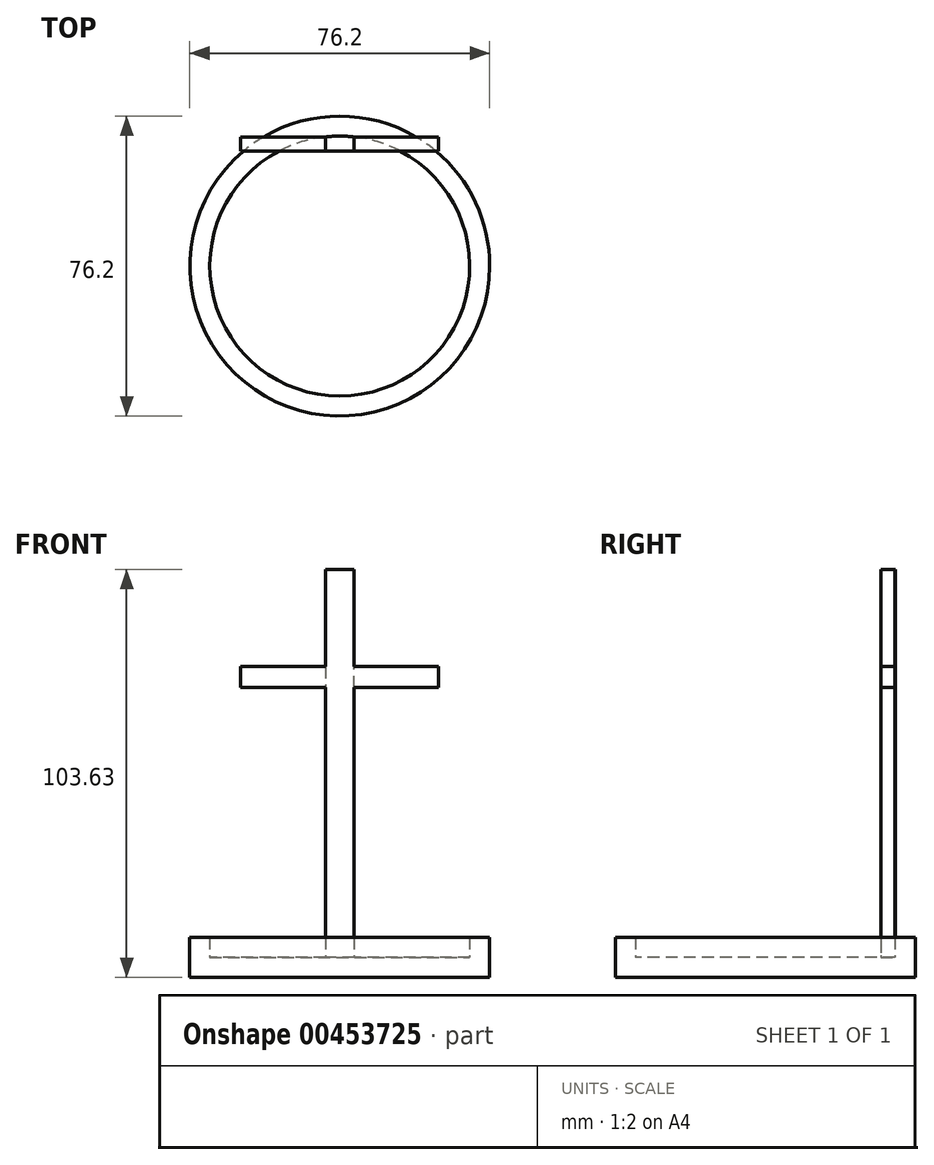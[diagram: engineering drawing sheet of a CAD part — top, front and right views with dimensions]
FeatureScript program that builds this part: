
annotation { "Feature Type Name" : "Feature", "Feature Type Description" : "" }
export const myFeature = defineFeature(function(context is Context, id is Id, definition is map)
    precondition{}
    {
        {
            var Q0;
            Q0=qCreatedBy(makeId("Top.planeOp"),FACE);
            var sketch = newSketch(context, id + "F0", { "sketchPlane" : qUnion([Q0])});
            skCircle(sketch, "E0", {"center": v(0, 0) * mm, "radius": 38.1 * mm});
            skSolve(sketch);
        }
        {
            var Q0;
            Q0=makeQuery(id+"F0.imprint","IMPRINT",FACE,{"disambiguationData":[TD([[makeQuery(id+"F0.imprint","IMPRINT",EDGE,{"derivedFrom":sQuery(id+"F0.wireOp",EDGE,"E0")}),1.0]])]});
            extrude(context, id + "F1", {"entities" : qUnion([Q0]), "depth" : 10.16 * mm});
        }
        {
            var Q0;
            Q0=makeQuery(id+"F1.opExtrude","CAP_FACE",FACE,{"disambiguationData":[OSD([sQuery(id+"F0.wireOp",EDGE,"E0")])],"isStart":false});
            shell(context, id + "F2", {"entities" : qUnion([Q0]), "thickness" : 5.08 * mm});
        }
        {
            var Q0;
            {var subQ0=sQuery(id+"F0.wireOp",EDGE,"E0");Q0=makeQuery(id+"F2.opShell","OFFSET_FACE",FACE,{"disambiguationData":[OSD([subQ0]),TDD([makeQuery(id+"F1.opExtrude","CAP_FACE",FACE,{"disambiguationData":[OSD([subQ0])],"isStart":true})])]});}
            var sketch = newSketch(context, id + "F3", { "sketchPlane" : qUnion([Q0])});
            skLineSegment(sketch, "E1.bottom", {"start": v(3.64, 29.24) * mm, "end": v(-3.64, 29.24) * mm});
            skLineSegment(sketch, "E1.top", {"start": v(3.64, 33.91) * mm, "end": v(-3.64, 33.91) * mm});
            skLineSegment(sketch, "E1.left", {"start": v(3.64, 29.24) * mm, "end": v(3.64, 33.91) * mm});
            skLineSegment(sketch, "E1.right", {"start": v(-3.64, 29.24) * mm, "end": v(-3.64, 33.91) * mm});
            skPoint(sketch, "E1.middle", {"position": v(0, 31.58) * mm});
            skSolve(sketch);
        }
        {
            var Q0;
            Q0=makeQuery(id+"F3.imprint","IMPRINT",FACE,{"disambiguationData":[TD([[makeQuery(id+"F3.imprint","IMPRINT",EDGE,{"derivedFrom":sQuery(id+"F3.wireOp",EDGE,"E1.bottom")}),-1.0]])]});
            extrude(context, id + "F4", {"entities" : qUnion([Q0]), "operationType" : NewBodyOperationType.ADD, "depth" : 98.55 * mm});
        }
        {
            var Q0;
            Q0=qCreatedBy(makeId("Right.planeOp"),FACE);
            var sketch = newSketch(context, id + "F5", { "sketchPlane" : qUnion([Q0])});
            skLineSegment(sketch, "E2.bottom", {"start": v(29.24, 73.62) * mm, "end": v(32.82, 73.62) * mm});
            skLineSegment(sketch, "E2.top", {"start": v(29.24, 78.97) * mm, "end": v(32.82, 78.97) * mm});
            skLineSegment(sketch, "E2.left", {"start": v(29.24, 73.62) * mm, "end": v(29.24, 78.97) * mm});
            skLineSegment(sketch, "E2.right", {"start": v(32.82, 73.62) * mm, "end": v(32.82, 78.97) * mm});
            skPoint(sketch, "E2.middle", {"position": v(31.03, 76.3) * mm});
            skSolve(sketch);
        }
        {
            var Q0;
            Q0 = qSketchRegion(id + "F5", true);
            extrude(context, id + "F6", {"entities" : qUnion([Q0]), "operationType" : NewBodyOperationType.ADD, "endBound" : BoundingType.SYMMETRIC, "depth" : 50.3 * mm});
        }
    });
